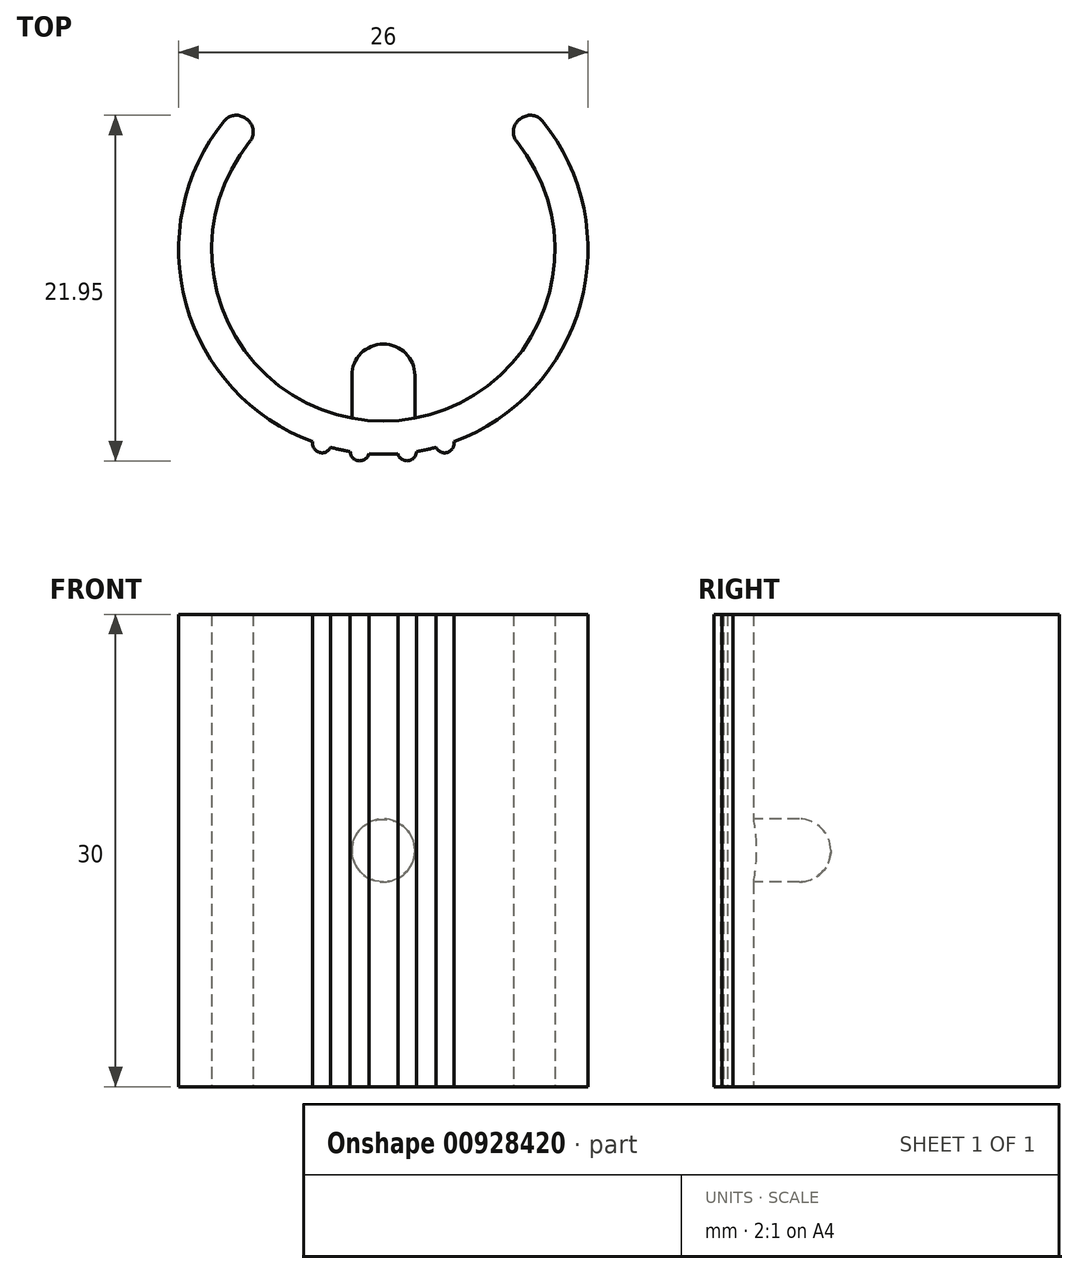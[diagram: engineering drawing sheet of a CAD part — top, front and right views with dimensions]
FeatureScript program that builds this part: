
annotation { "Feature Type Name" : "Feature", "Feature Type Description" : "" }
export const myFeature = defineFeature(function(context is Context, id is Id, definition is map)
    precondition{}
    {
        {
            var Q0;
            Q0=qCreatedBy(makeId("Top.planeOp"),FACE);
            var sketch = newSketch(context, id + "F0", { "sketchPlane" : qUnion([Q0])});
            skArc(sketch, "E0", {"start": v(-10.12, 8.16) * mm, "mid": v(-12.53, -3.47) * mm, "end": v(-4.49, -12.2) * mm});
            skArc(sketch, "E1", {"start": v(-8.48, 6.85) * mm, "mid": v(0, -10.9) * mm, "end": v(8.48, 6.85) * mm});
            skLineSegment(sketch, "E2", {"start": v(-8.72, 8.32) * mm, "end": v(-8.8, 8.37) * mm});
            skLineSegment(sketch, "E3.MirrorCS", {"start": v(8.72, 8.32) * mm, "end": v(8.8, 8.37) * mm});
            skPoint(sketch, "E4.visualSharp", {"position": v(-7.73, 7.68) * mm});
            skArc(sketch, "E4.filletArc", {"start": v(-8.48, 6.85) * mm, "mid": v(-8.27, 7.64) * mm, "end": v(-8.72, 8.32) * mm});
            skPoint(sketch, "E5.visualSharp", {"position": v(-9.53, 8.84) * mm});
            skArc(sketch, "E5.filletArc", {"start": v(-8.8, 8.37) * mm, "mid": v(-9.5, 8.52) * mm, "end": v(-10.12, 8.16) * mm});
            skArc(sketch, "E6.MirrorCS", {"start": v(8.48, 6.85) * mm, "mid": v(8.27, 7.64) * mm, "end": v(8.72, 8.32) * mm});
            skPoint(sketch, "E7.MirrorP", {"position": v(9.53, 8.84) * mm});
            skArc(sketch, "E8.MirrorCS", {"start": v(8.8, 8.37) * mm, "mid": v(9.5, 8.52) * mm, "end": v(10.12, 8.16) * mm});
            skPoint(sketch, "E9.orphan", {"position": v(7.73, 7.68) * mm});
            skArc(sketch, "E10", {"start": v(-2.1, -12.83) * mm, "mid": v(-1.57, -13.41) * mm, "end": v(-0.92, -12.97) * mm});
            skArc(sketch, "E11", {"start": v(-4.49, -12.2) * mm, "mid": v(-4.08, -12.88) * mm, "end": v(-3.35, -12.56) * mm});
            skArc(sketch, "E12.MirrorCS", {"start": v(2.1, -12.83) * mm, "mid": v(1.57, -13.41) * mm, "end": v(0.92, -12.97) * mm});
            skArc(sketch, "E13.MirrorCS", {"start": v(4.49, -12.2) * mm, "mid": v(4.08, -12.88) * mm, "end": v(3.35, -12.56) * mm});
            skArc(sketch, "E14.trimOffspring", {"start": v(-0.92, -12.97) * mm, "mid": v(0, -13) * mm, "end": v(0.92, -12.97) * mm});
            skArc(sketch, "E15.trimOffspring", {"start": v(-3.35, -12.56) * mm, "mid": v(-2.73, -12.71) * mm, "end": v(-2.1, -12.83) * mm});
            skArc(sketch, "E16.trimOffspring", {"start": v(2.1, -12.83) * mm, "mid": v(2.73, -12.71) * mm, "end": v(3.35, -12.56) * mm});
            skArc(sketch, "E17.trimOffspring", {"start": v(4.49, -12.2) * mm, "mid": v(12.53, -3.47) * mm, "end": v(10.12, 8.16) * mm});
            skSolve(sketch);
        }
        {
            var Q0;
            Q0 = qSketchRegion(id + "F0", true);
            extrude(context, id + "F1", {"entities" : qUnion([Q0]), "depth" : 15 * mm, "offsetDistance" : 25 * mm, "hasSecondDirection" : true, "secondDirectionOppositeDirection" : true, "secondDirectionDepth" : 15 * mm});
        }
        {
            var Q0;
            Q0=qCreatedBy(makeId("Front.planeOp"),FACE);
            cPlane(context, id + "F2", {"entities" : qUnion([Q0]), "cplaneType" : CPlaneType.OFFSET, "offset" : 11.5 * mm, "width" : 150 * mm, "height" : 150 * mm});
        }
        {
            var Q0;
            Q0=qCreatedBy(id+"F2.planeOp",FACE);
            var sketch = newSketch(context, id + "F3", { "sketchPlane" : qUnion([Q0])});
            skCircle(sketch, "E18", {"center": v(0, 0) * mm, "radius": 2 * mm});
            skSolve(sketch);
        }
        {
            var Q0;
            Q0 = qSketchRegion(id + "F3", true);
            extrude(context, id + "F4", {"entities" : qUnion([Q0]), "operationType" : NewBodyOperationType.ADD, "oppositeDirection" : true, "depth" : 5.5 * mm, "offsetDistance" : 25 * mm});
        }
        {
            var Q0;
            Q0=makeQuery(id+"F4.opExtrude","CAP_EDGE",EDGE,{"disambiguationData":[OSD([sQuery(id+"F3.wireOp",EDGE,"E18")])],"isStart":false});
            fillet(context, id + "F5", {"entities" : qUnion([Q0]), "radius" : 2 * mm, "tangentPropagation" : true, "allowEdgeOverflow" : false});
        }
    });
